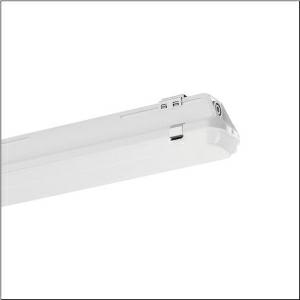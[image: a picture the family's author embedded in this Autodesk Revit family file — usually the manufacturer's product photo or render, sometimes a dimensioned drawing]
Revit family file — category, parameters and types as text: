
# Revit family: monsun_r__21_51fb107l440k_cbf5
name_source: partatom
category: Lighting Fixtures
units: mm (PartAtom-declared; Revit-internal decimal feet)

## family parameters
Cut with Voids When Loaded = No
Host = Face
Light Source = No
Part Type = Normal
Room Calculation Point = No
Round Connector Dimension = Use Diameter
Shared = No

## types (1)
- Monsun® 21 (1 x LED, 4350 lm, 24.7 W, 4000K)
    Apparent Load = 25 VA
    CIE Flux Codes = 46 76 93 94 100
    Color Rendering = 80
    Color Temperature = 4000K
    Default Elevation = 1800 mm
    Description = Monsun® 21, damp-proof luminaire, chain hanger, primary optical cover: enclosure, of PMMA, light emission: direct distribution, primary light characteristic: symmetric, installation type: suspended mounting, surface-mounted, horizontal mounting, vertical mounting, LED, rated luminous flux: 4.350lm, luminous efficacy: 176lm/W, light colour: 840, colour temperature: 4000K, control gear: ON/OFF, with terminal, 3-pole, max. 2.5mm², mains connection: 220..240V, AC, 50/60Hz, rated input power: 25W, housing, of glass-fibre reinforced plastic, uncoated, bright grey, incl. chain hanger, length: 1.299mm, width: 90mm, height: 88mm, clip for enclosure, of stainless steel (V2A), ceiling mounting element, of stainless steel (V2A), chain hanger, of stainless steel (V2A), protection rating (complete): IP66, insulation class (complete): insulation class I (protective earthing), certification: CE, ENEC, VDE, UKCA, protection symbol: D, impact resistance: IK04, permissible operating ambient temperature: -25..+35°C, standard: EN 50419, EN 60598-2-1, corresponds to IFS (International Featured Standards) requirements for safety and quality in the food industry, for indoor or canopied outdoor use, no direct snow, no direct sun, no direct rain, LABS conformity tested according to VDMA 24364:2018-05, contact your sales advisor before using the luminaires in applications with unclear chemical exposure, large temperature fluctuations or condensation-forming humidity, packaging unit: 1 piece
    Height = 88 mm
    Lamp = 1 x LED
    Lamp Light Flux = 4350 lm
    Lamp Power = 24.7 W
    Lamp count = 1
    Length = 1299 mm
    Luminous efficacy = 176 lm/W
    Manufacturer = Siteco
    ModVariant = No
    Model = 51FB107L440K
    Mounting Place = Ceiling
    Mounting Type = Surface mounted
    Number of Poles = 1
    OnlyDefault = Yes
    Power Factor = 1
    Product Name = Monsun® 21
    Product group = damp-proof luminaire
    ProductGroupID = 300
    Protection Class = Protection class I
    Protection Degree = IP 66
    RLX_Detail_Level = 1
    RLX_Emergency_Light_Flux = 0 lm
    RLX_Emergency_Type = 0
    RLX_Emergency_Type_DB = No
    RlxData = <blob elided: 89685 chars, md5=d9e1a508>
    Socket = socket
    Standby Power = 0 W
    System Light Flux = 4350 lm
    System Power = 25 W
    Type Comments = Product without accessories
    Type Image = l_1319656.jpg
    URL = http://relux.com
    VarID = ---
    Voltage = 0 V
    Weight = 0.00 kg
    Width = 90 mm

## geometry (parser evidence)
native form markers: Blend x4, Sweep x13
no freeform markers — native parametric forms only
